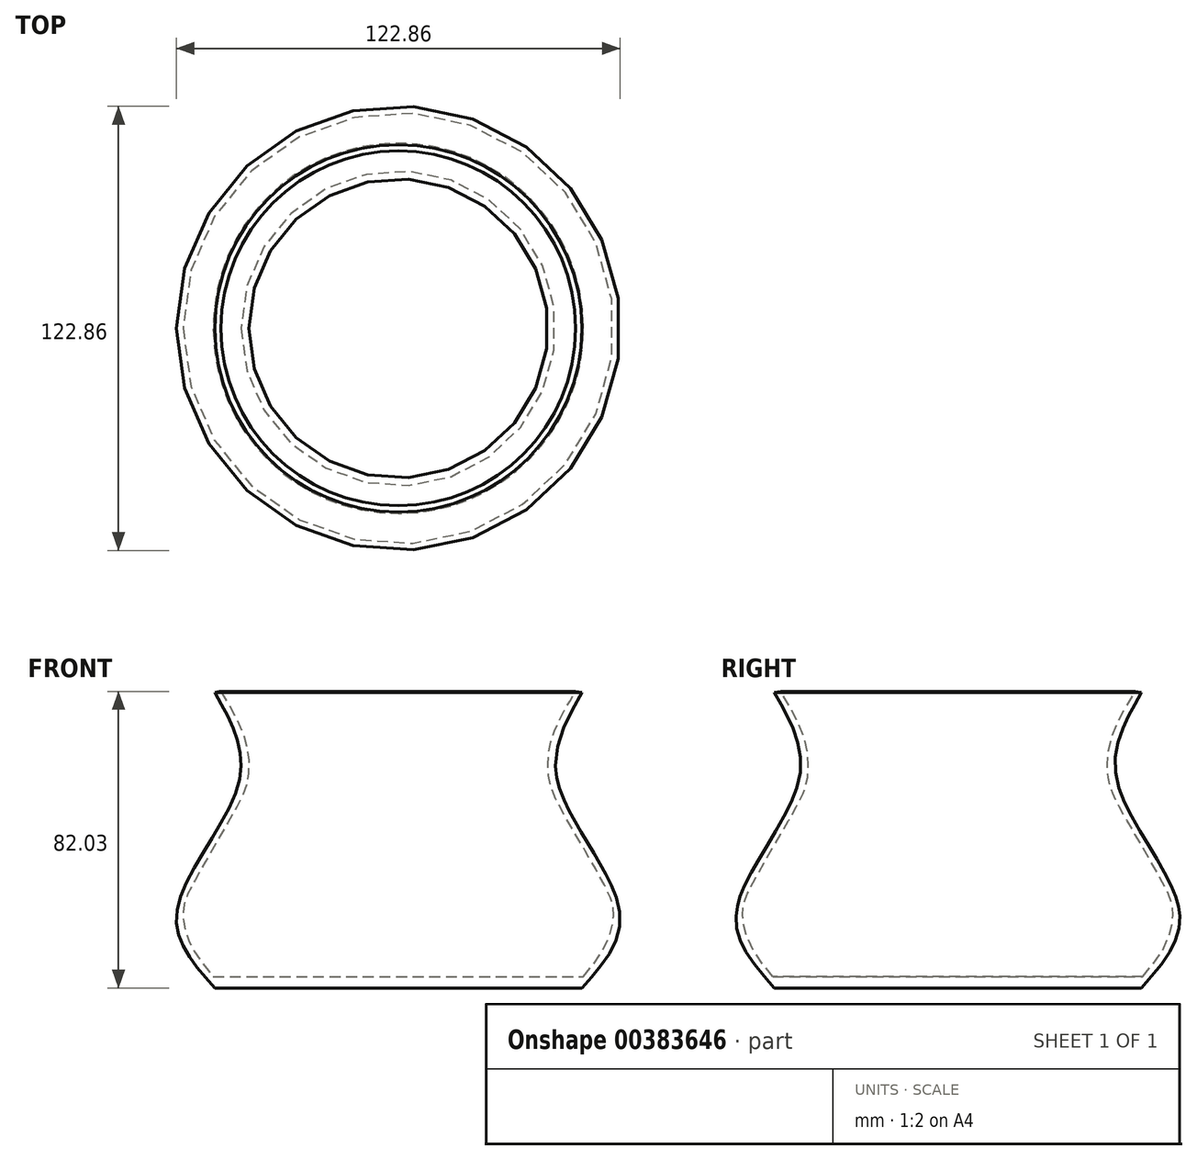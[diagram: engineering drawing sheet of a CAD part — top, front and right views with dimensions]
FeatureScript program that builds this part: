
annotation { "Feature Type Name" : "Feature", "Feature Type Description" : "" }
export const myFeature = defineFeature(function(context is Context, id is Id, definition is map)
    precondition{}
    {
        {
            var Q0;
            Q0=qCreatedBy(makeId("Front.planeOp"),FACE);
            var sketch = newSketch(context, id + "F0", { "sketchPlane" : qUnion([Q0])});
            skLineSegment(sketch, "E0", {"start": v(0, 0) * mm, "end": v(-50.8, 0) * mm});
            skFitSpline(sketch, "E1", {"points": [v(-50.8, 0) * mm, v(-61.3, 21.13) * mm, v(-44.08, 57.06) * mm, v(-50.8, 81.7) * mm], "startDerivative": vector(-58.05, 64.58) * mm, "endDerivative": vector(-42.85, 74.42) * mm});
            skLineSegment(sketch, "E2", {"start": v(0, 0) * mm, "end": v(0, 3.18) * mm});
            skLineSegment(sketch, "E3", {"start": v(0, 3.18) * mm, "end": v(-51.22, 3.18) * mm});
            skFitSpline(sketch, "E4", {"points": [v(-49.08, 82.03) * mm, v(-42.38, 68.62) * mm, v(-41.65, 57.94) * mm, v(-45.28, 49.06) * mm, v(-58.14, 26.24) * mm, v(-59.59, 20.8) * mm, v(-58.68, 15) * mm, v(-55.42, 8.48) * mm, v(-51.22, 3.17) * mm], "startDerivative": vector(53.22, -87.8) * mm, "endDerivative": vector(42.54, -49.66) * mm});
            skLineSegment(sketch, "E5", {"start": v(-49.08, 82.03) * mm, "end": v(-50.8, 81.7) * mm});
            skSolve(sketch);
        }
        {
            var Q0;
            Q0 = qSketchRegion(id + "F0", true);
            var Q1;
            Q1=sQuery(id+"F0.wireOp",EDGE,"E2");
            revolve(context, id + "F1", {"entities" : qUnion([Q0]), "axis" : qUnion([Q1]), "revolveType" : RevolveType.FULL});
        }
    });
